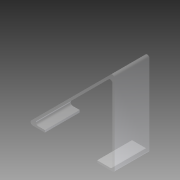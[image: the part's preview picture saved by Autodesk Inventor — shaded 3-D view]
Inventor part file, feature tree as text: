
AUTODESK INVENTOR PART (.ipt)
format: ipt  version: 2012 (Build 160160000, 160)  size: 97,280 bytes
history: native  units: in
note: dims shown in document units (in); Inventor stores cm internally (conversion verified against a paired STEP export)
features: extrude x1, fillet x1, sketch x1
ambient origin geometry x8: Origin, YZ Plane, XZ Plane, XY Plane, X Axis, Y Axis, Z Axis, Center Point
bodies: Solid1 (feature_tree)
feature tree (3):
  extrude  "Extrusion1"  Depth=5.0in
  fillet  "Fillet1"  Radius=1.0in
  sketch  "Sketch1"  dims[d0=5.0in d1=5.0in d2=1.0in d4=0.125in d5=0.125in d6=0.125in d7=1.0in d8=0.125in d9=2.0in d10=0.0in d11=0.125in]
